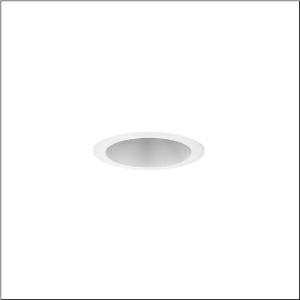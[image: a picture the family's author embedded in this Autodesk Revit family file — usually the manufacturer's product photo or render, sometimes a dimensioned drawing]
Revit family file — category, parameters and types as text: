
# Revit family: lunis_31_mini_51dn167e31
name_source: partatom
category: Lighting Fixtures
units: mm (PartAtom-declared; Revit-internal decimal feet)

## family parameters
Cut with Voids When Loaded = No
Host = Face
Light Source = No
Part Type = Normal
Room Calculation Point = No
Round Connector Dimension = Use Diameter
Shared = No

## types (1)
- Lunis 31 mini (1 x LED, 1000 lm, 8.3 W, 3000K)
    Apparent Load = 8 VA
    CIE Flux Codes = 69 93 99 100 100
    Color Rendering = 80
    Color Temperature = 3000K
    Default Elevation = 1800 mm
    Description = Lunis 31,  mini, downlight, light control with reflector, light emission: direct distribution, LED rated luminous flux: 1.000lm, light colour: 830, mains connection: 220..240V, AC, 50/60Hz, housing, white, protection rating (complete): IP20, protection rating (on room side): IP54, insulation class (complete): insulation class II (safety insulation), certification: CE, packaging unit: 1 piece
    Height = 0 mm  [stored 0 ft]
    Lamp = 1 x LED
    Lamp Light Flux = 1000 lm
    Lamp Power = 8.3 W
    Lamp count = 1
    Length = 188 mm  [stored 0.616798 ft]
    Luminous efficacy = 120 lm/W
    Manufacturer = Siteco
    ModVariant = No
    Model = 51DN167E31
    Mounting Place = Ceiling
    Mounting Type = Recessed
    Number of Poles = 1
    OnlyDefault = Yes
    Power Factor = 1
    Product Name = Lunis 31 mini
    Product group = downlight
    ProductGroupID = 400
    Protection Class = Protection class II
    Protection Degree = IP 20
    RLX_Detail_Level = 1
    RLX_Emergency_Light_Flux = 0 lm
    RLX_Emergency_Type = 0
    RLX_Emergency_Type_DB = No
    RlxData = <blob elided: 21733 chars, md5=85b58bd2>
    Socket = socket
    Standby Power = 0 W
    System Light Flux = 1000 lm
    System Power = 8 W
    Type Comments = Product without accessories
    Type Image = l_1005624.jpg
    URL = http://relux.com
    VarID = ---
    Voltage = 0 V
    Weight = 0.00 kg
    Width = 0 mm  [stored 0 ft]

note: [stored X ft] marks values corroborated as IEEE doubles in the binary element streams (Revit-internal decimal feet)

## geometry (parser evidence)
native form markers: Blend x4, Sweep x11
no freeform markers — native parametric forms only
